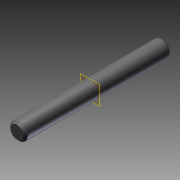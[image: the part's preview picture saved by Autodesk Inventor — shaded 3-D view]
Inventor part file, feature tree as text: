
AUTODESK INVENTOR PART (.ipt)
format: ipt  version: 2013 (Build 170138000, 138)  size: 76,288 bytes
history: native  units: mm (DEFAULTED — no unit token found)
features: imported_body x1, plane x1
ambient origin geometry x8: Origin, YZ Plane, XZ Plane, XY Plane, X Axis, Y Axis, Z Axis, Center Point
bodies: Solid1 (feature_tree)
feature tree (2):
  imported_body  "Base1"
  plane  "Work Plane1"
